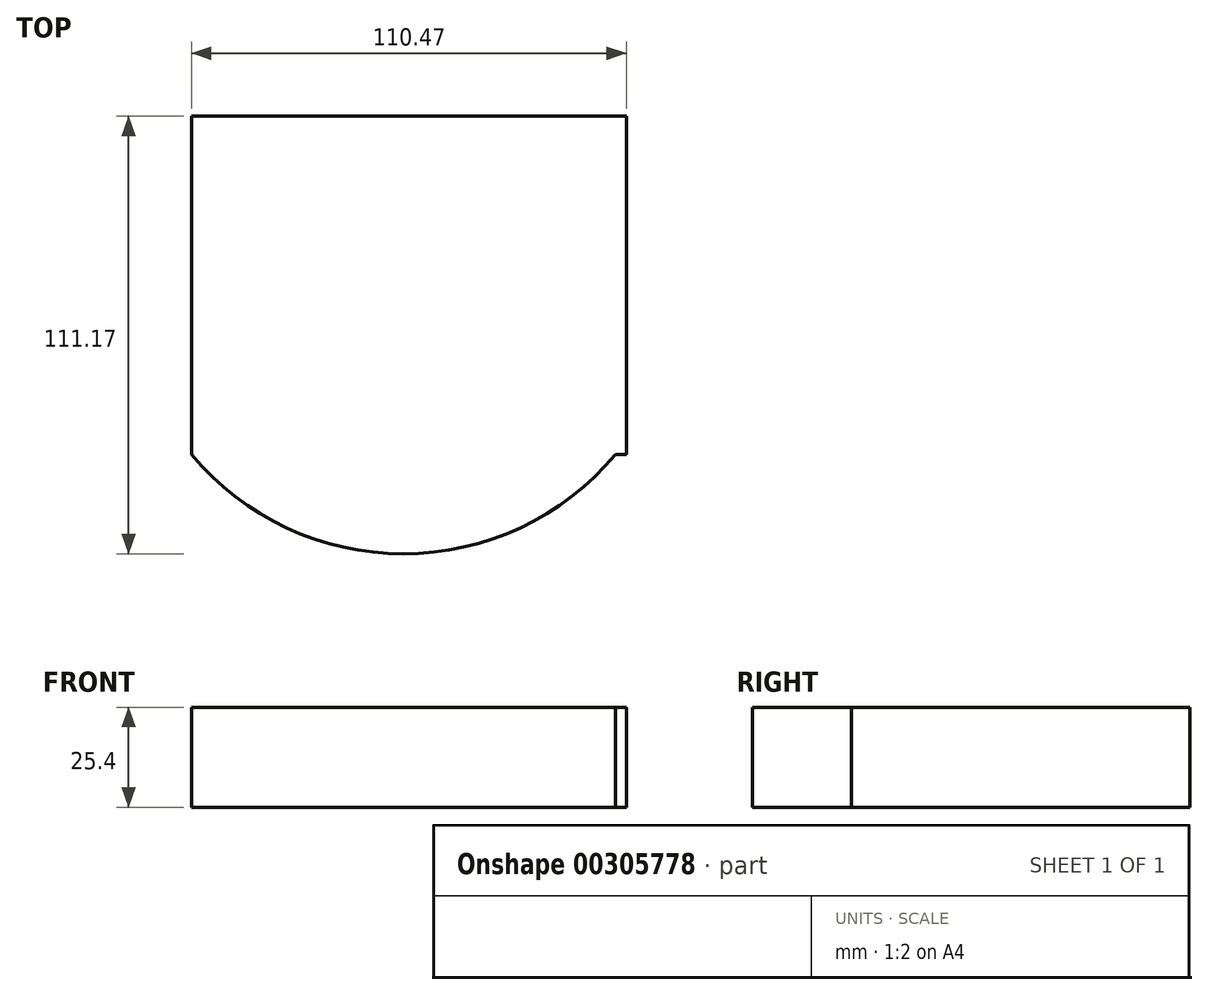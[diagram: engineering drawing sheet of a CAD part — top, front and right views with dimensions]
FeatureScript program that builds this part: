
annotation { "Feature Type Name" : "Feature", "Feature Type Description" : "" }
export const myFeature = defineFeature(function(context is Context, id is Id, definition is map)
    precondition{}
    {
        {
            var Q0;
            Q0=qCreatedBy(makeId("Top.planeOp"),FACE);
            var sketch = newSketch(context, id + "F0", { "sketchPlane" : qUnion([Q0])});
            skLineSegment(sketch, "E0.bottom", {"start": v(58.66, -47.88) * mm, "end": v(-51.8, -47.88) * mm});
            skLineSegment(sketch, "E0.top", {"start": v(58.66, 38.1) * mm, "end": v(-51.8, 38.1) * mm});
            skLineSegment(sketch, "E0.left", {"start": v(58.66, -47.88) * mm, "end": v(58.66, 38.1) * mm});
            skLineSegment(sketch, "E0.right", {"start": v(-51.8, -47.88) * mm, "end": v(-51.8, 38.1) * mm});
            skArc(sketch, "E1", {"start": v(-51.8, -47.88) * mm, "mid": v(4.3, -73.04) * mm, "end": v(58.66, -44.3) * mm});
            skSolve(sketch);
        }
        {
            var Q0;
            Q0 = qSketchRegion(id + "F0", true);
            extrude(context, id + "F1", {"entities" : qUnion([Q0]), "depth" : 25.4 * mm});
        }
    });
